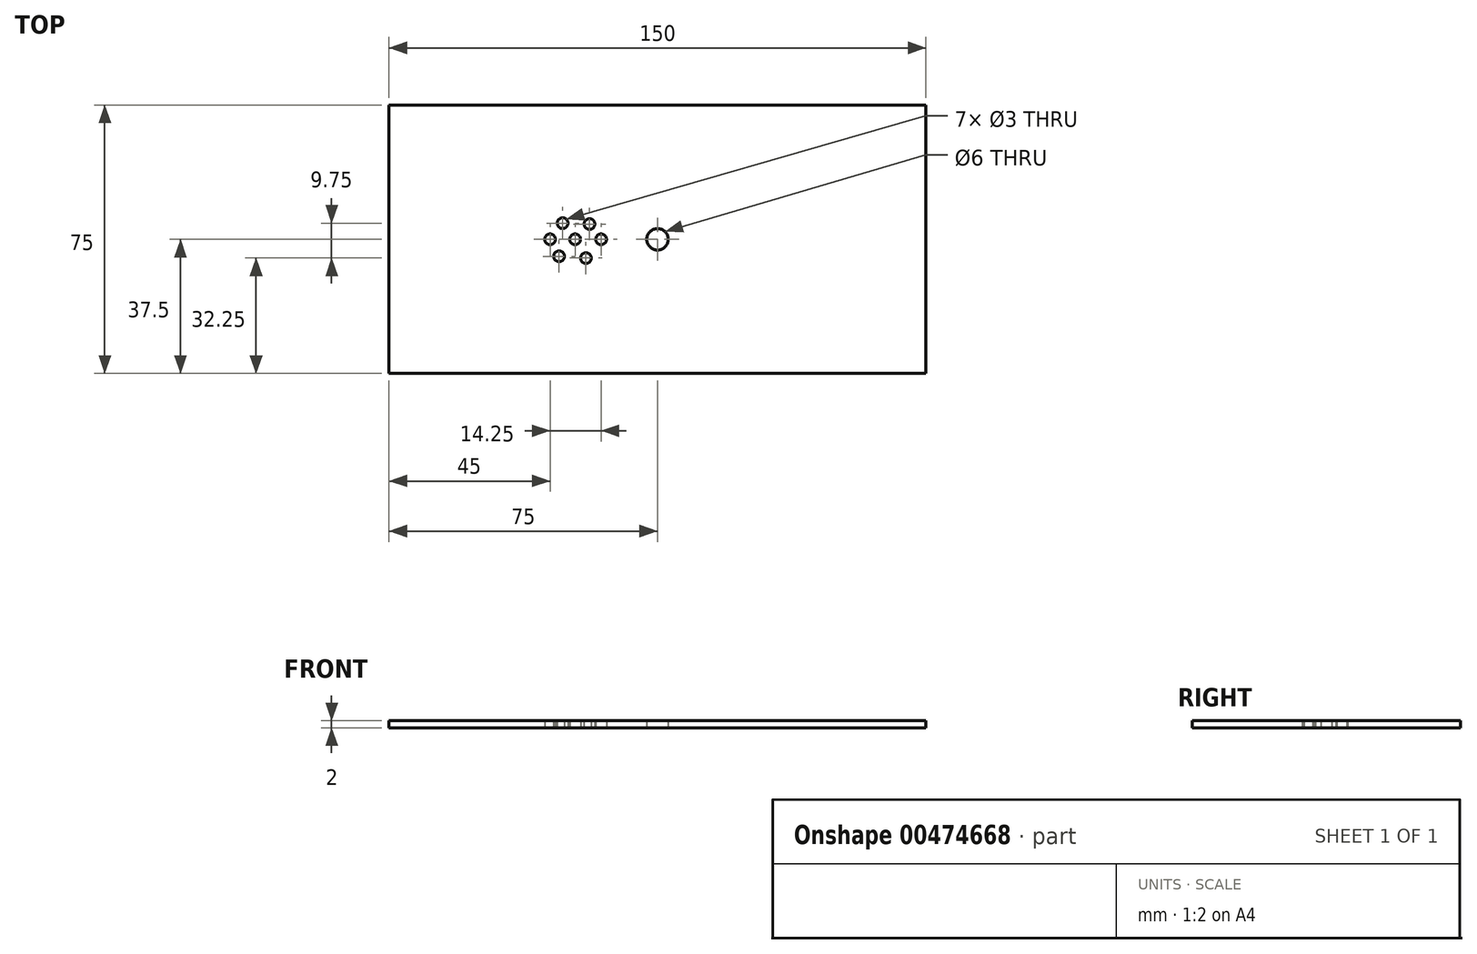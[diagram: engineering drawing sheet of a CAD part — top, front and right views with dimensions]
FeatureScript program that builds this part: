
annotation { "Feature Type Name" : "Feature", "Feature Type Description" : "" }
export const myFeature = defineFeature(function(context is Context, id is Id, definition is map)
    precondition{}
    {
        {
            var Q0;
            Q0=qCreatedBy(makeId("Top.planeOp"),FACE);
            var sketch = newSketch(context, id + "F0", { "sketchPlane" : qUnion([Q0])});
            skLineSegment(sketch, "E0.bottom", {"start": v(-75, 37.5) * mm, "end": v(75, 37.5) * mm});
            skLineSegment(sketch, "E0.top", {"start": v(-75, -37.5) * mm, "end": v(75, -37.5) * mm});
            skLineSegment(sketch, "E0.left", {"start": v(-75, 37.5) * mm, "end": v(-75, -37.5) * mm});
            skLineSegment(sketch, "E0.right", {"start": v(75, 37.5) * mm, "end": v(75, -37.5) * mm});
            skPoint(sketch, "E0.middle", {"position": v(0, 0) * mm});
            skCircle(sketch, "E1", {"center": v(0, 0) * mm, "radius": 3 * mm});
            skCircle(sketch, "E2", {"center": v(-26.5, 4.5) * mm, "radius": 1.5 * mm});
            skCircle(sketch, "E3", {"center": v(-30, 0) * mm, "radius": 1.5 * mm});
            skCircle(sketch, "E4", {"center": v(-23, 0) * mm, "radius": 1.5 * mm});
            skCircle(sketch, "E5", {"center": v(-27.5, -4.75) * mm, "radius": 1.5 * mm});
            skCircle(sketch, "E6", {"center": v(-20, -5.25) * mm, "radius": 1.5 * mm});
            skCircle(sketch, "E7", {"center": v(-15.75, 0) * mm, "radius": 1.5 * mm});
            skCircle(sketch, "E8", {"center": v(-19, 4.25) * mm, "radius": 1.5 * mm});
            skSolve(sketch);
        }
        {
            var Q0;
            Q0 = qSketchRegion(id + "F0", true);
            extrude(context, id + "F1", {"entities" : qUnion([Q0]), "depth" : 2 * mm});
        }
    });
